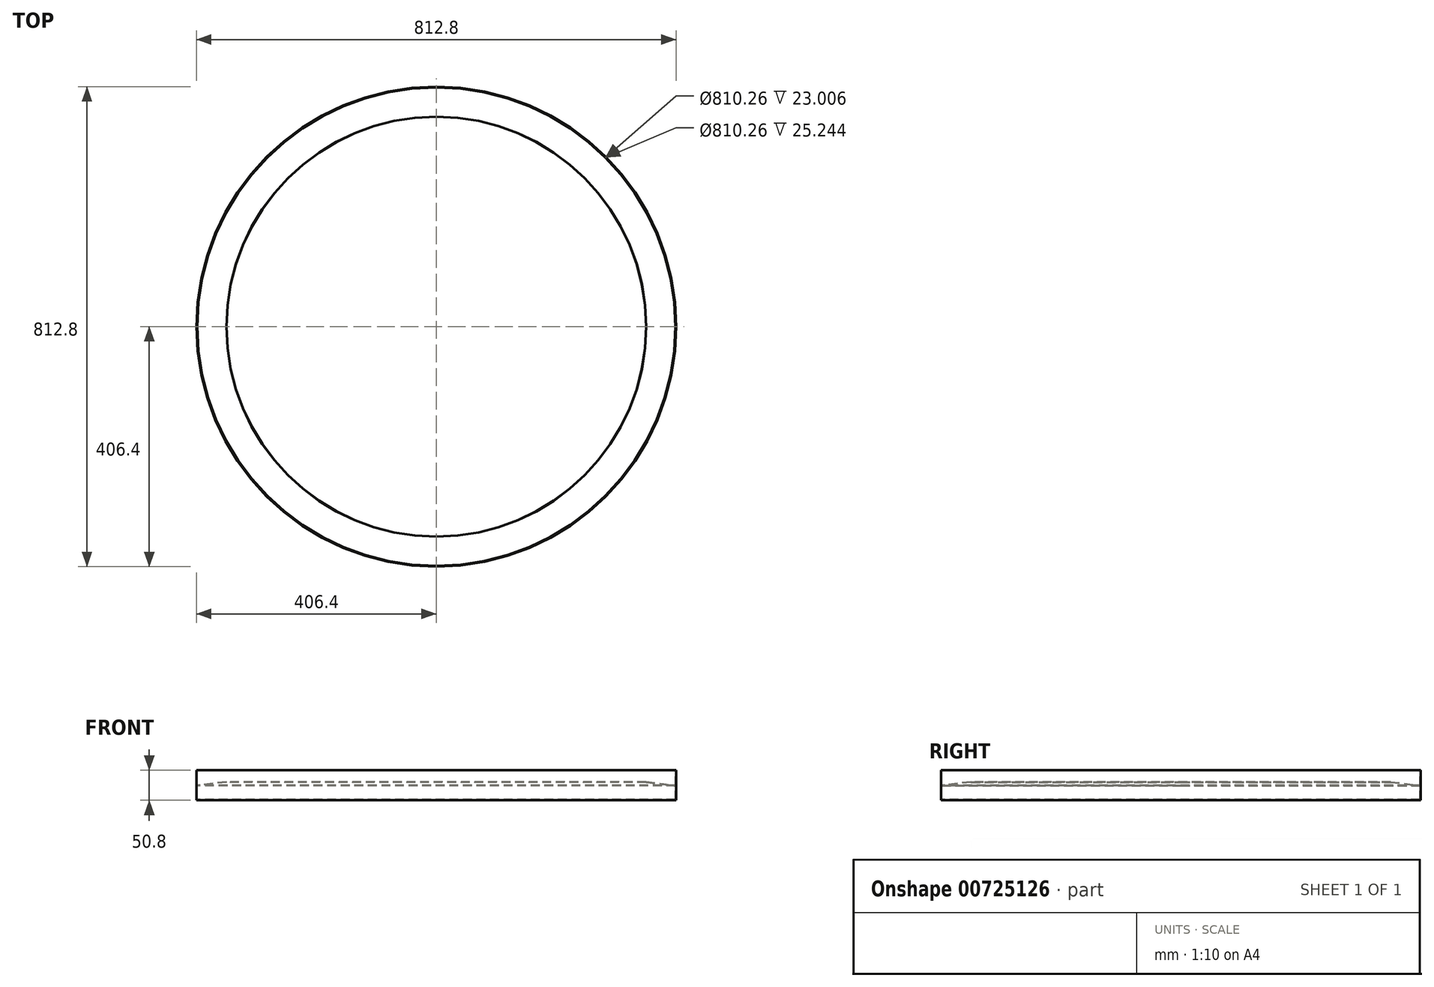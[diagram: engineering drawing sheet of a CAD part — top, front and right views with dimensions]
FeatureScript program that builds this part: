
annotation { "Feature Type Name" : "Feature", "Feature Type Description" : "" }
export const myFeature = defineFeature(function(context is Context, id is Id, definition is map)
    precondition{}
    {
        {
            var Q0;
            Q0=qCreatedBy(makeId("Front.planeOp"),FACE);
            var sketch = newSketch(context, id + "F0", { "sketchPlane" : qUnion([Q0])});
            skLineSegment(sketch, "E0.left", {"start": v(-406.4, -3.12) * mm, "end": v(-406.4, -28.52) * mm});
            skLineSegment(sketch, "E1", {"start": v(-355.7, 3.1) * mm, "end": v(-405.13, -2.96) * mm});
            skLineSegment(sketch, "E2", {"start": v(-355.7, 3.1) * mm, "end": v(-355.54, 1.85) * mm});
            skLineSegment(sketch, "E3", {"start": v(-355.54, 1.85) * mm, "end": v(-405.13, -4.24) * mm});
            skPoint(sketch, "E4.orphan", {"position": v(-406.4, 0) * mm});
            skLineSegment(sketch, "E5", {"start": v(-406.4, -3.12) * mm, "end": v(-406.4, 22.28) * mm});
            skLineSegment(sketch, "E6", {"start": v(-406.4, 22.28) * mm, "end": v(-405.13, 22.28) * mm});
            skLineSegment(sketch, "E7", {"start": v(-405.13, 22.28) * mm, "end": v(-405.13, -2.96) * mm});
            skLineSegment(sketch, "E8", {"start": v(-406.4, -28.52) * mm, "end": v(0, -28.52) * mm});
            skLineSegment(sketch, "E9", {"start": v(-405.13, -27.25) * mm, "end": v(-405.13, -4.24) * mm});
            skLineSegment(sketch, "E10", {"start": v(-405.13, -27.25) * mm, "end": v(0, -27.25) * mm});
            skLineSegment(sketch, "E11", {"start": v(0, -28.52) * mm, "end": v(0, -27.25) * mm});
            skSolve(sketch);
        }
        {
            var Q0;
            Q0=qCreatedBy(makeId("Front.planeOp"),FACE);
            var sketch = newSketch(context, id + "F1", { "sketchPlane" : qUnion([Q0])});
            skLineSegment(sketch, "E12", {"start": v(0, 40.5) * mm, "end": v(0, -62.38) * mm});
            skSolve(sketch);
        }
        {
            var Q0;
            Q0=makeQuery(id+"F0.imprint","IMPRINT",FACE,{"disambiguationData":[TD([[makeQuery(id+"F0.imprint","IMPRINT",EDGE,{"derivedFrom":sQuery(id+"F0.wireOp",EDGE,"E0.left")}),1.0]])]});
            var Q1;
            Q1=sQuery(id+"F1.wireOp",EDGE,"E12");
            revolve(context, id + "F2", {"surfaceOperationType" : NewSurfaceOperationType.NEW, "entities" : qUnion([Q0]), "axis" : qUnion([Q1]), "revolveType" : RevolveType.FULL});
        }
    });
